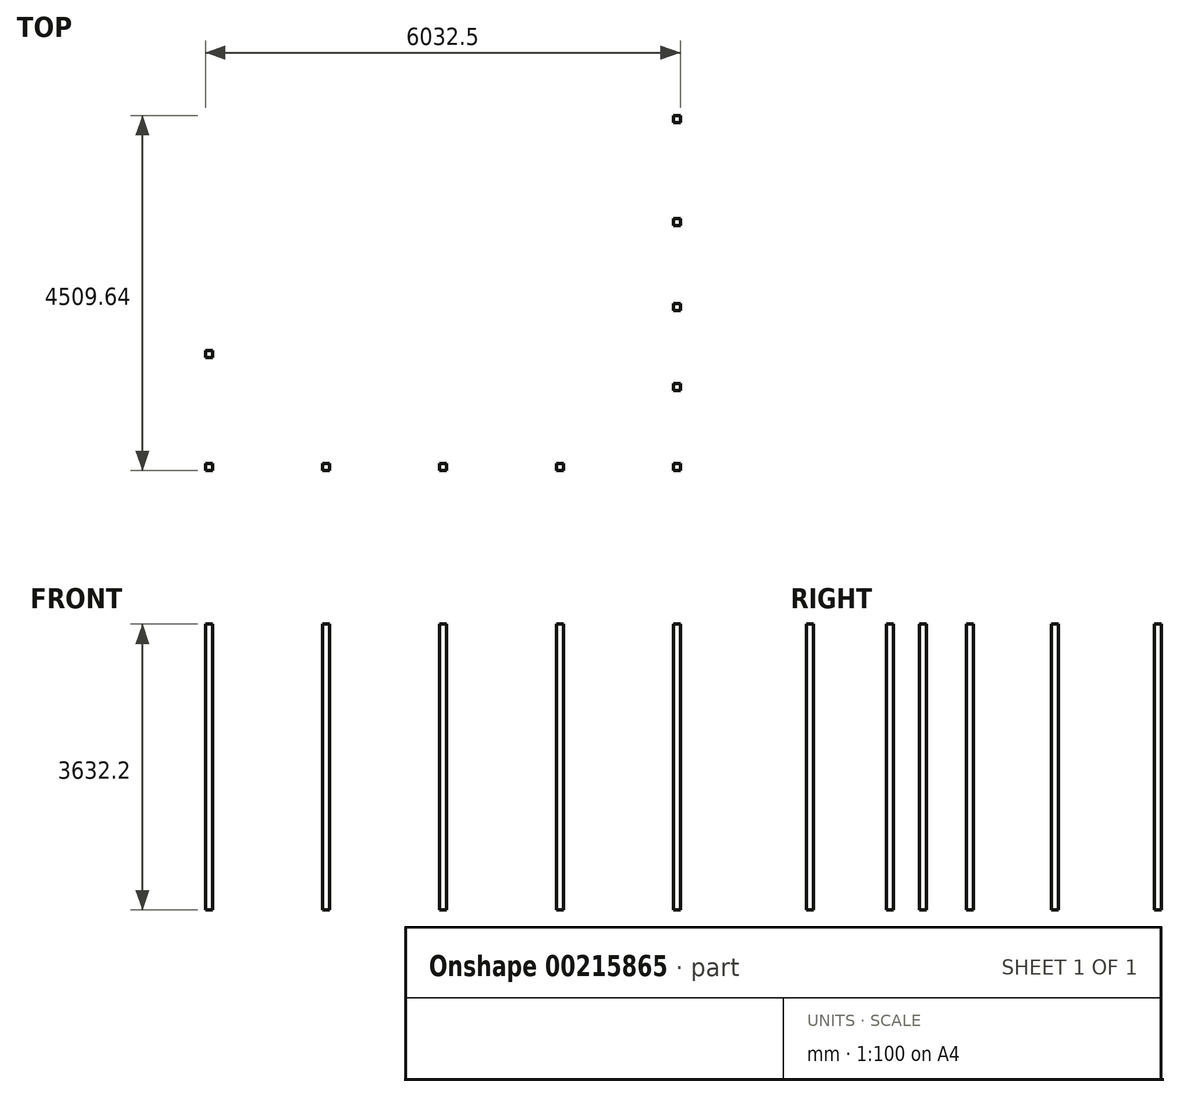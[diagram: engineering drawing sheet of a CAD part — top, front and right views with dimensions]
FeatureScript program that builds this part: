
annotation { "Feature Type Name" : "Feature", "Feature Type Description" : "" }
export const myFeature = defineFeature(function(context is Context, id is Id, definition is map)
    precondition{}
    {
        {
            var Q0;
            Q0=qCreatedBy(makeId("Top.planeOp"),FACE);
            var sketch = newSketch(context, id + "F0", { "sketchPlane" : qUnion([Q0])});
            skLineSegment(sketch, "E0.bottom", {"start": v(0, 0) * mm, "end": v(-88.9, 0) * mm});
            skLineSegment(sketch, "E0.top", {"start": v(0, 88.9) * mm, "end": v(-88.9, 88.9) * mm});
            skLineSegment(sketch, "E0.left", {"start": v(0, 0) * mm, "end": v(0, 88.9) * mm});
            skLineSegment(sketch, "E0.right", {"start": v(-88.9, 0) * mm, "end": v(-88.9, 88.9) * mm});
            skLineSegment(sketch, "E1.bottom", {"start": v(-1485.9, 0) * mm, "end": v(-1574.8, 0) * mm});
            skLineSegment(sketch, "E1.top", {"start": v(-1485.9, 88.9) * mm, "end": v(-1574.8, 88.9) * mm});
            skLineSegment(sketch, "E1.left", {"start": v(-1485.9, 0) * mm, "end": v(-1485.9, 88.9) * mm});
            skLineSegment(sketch, "E1.right", {"start": v(-1574.8, 0) * mm, "end": v(-1574.8, 88.9) * mm});
            skLineSegment(sketch, "E2.bottom", {"start": v(-2971.8, 0) * mm, "end": v(-3060.7, 0) * mm});
            skLineSegment(sketch, "E2.top", {"start": v(-2971.8, 88.9) * mm, "end": v(-3060.7, 88.9) * mm});
            skLineSegment(sketch, "E2.left", {"start": v(-2971.8, 0) * mm, "end": v(-2971.8, 88.9) * mm});
            skLineSegment(sketch, "E2.right", {"start": v(-3060.7, 0) * mm, "end": v(-3060.7, 88.9) * mm});
            skLineSegment(sketch, "E3.bottom", {"start": v(-4457.7, 0) * mm, "end": v(-4546.6, 0) * mm});
            skLineSegment(sketch, "E3.top", {"start": v(-4457.7, 88.9) * mm, "end": v(-4546.6, 88.9) * mm});
            skLineSegment(sketch, "E3.left", {"start": v(-4457.7, 0) * mm, "end": v(-4457.7, 88.9) * mm});
            skLineSegment(sketch, "E3.right", {"start": v(-4546.6, 0) * mm, "end": v(-4546.6, 88.9) * mm});
            skLineSegment(sketch, "E4.bottom", {"start": v(-5943.6, 0) * mm, "end": v(-6032.5, 0) * mm});
            skLineSegment(sketch, "E4.top", {"start": v(-5943.6, 88.9) * mm, "end": v(-6032.5, 88.9) * mm});
            skLineSegment(sketch, "E4.left", {"start": v(-5943.6, 0) * mm, "end": v(-5943.6, 88.9) * mm});
            skLineSegment(sketch, "E4.right", {"start": v(-6032.5, 0) * mm, "end": v(-6032.5, 88.9) * mm});
            skLineSegment(sketch, "E5.bottom", {"start": v(-88.9, 1016) * mm, "end": v(0, 1016) * mm});
            skLineSegment(sketch, "E5.top", {"start": v(-88.9, 1104.9) * mm, "end": v(0, 1104.9) * mm});
            skLineSegment(sketch, "E5.left", {"start": v(-88.9, 1016) * mm, "end": v(-88.9, 1104.9) * mm});
            skLineSegment(sketch, "E5.right", {"start": v(0, 1016) * mm, "end": v(0, 1104.9) * mm});
            skLineSegment(sketch, "E6.bottom", {"start": v(-88.9, 2032) * mm, "end": v(0, 2032) * mm});
            skLineSegment(sketch, "E6.top", {"start": v(-88.9, 2120.9) * mm, "end": v(0, 2120.9) * mm});
            skLineSegment(sketch, "E6.left", {"start": v(-88.9, 2032) * mm, "end": v(-88.9, 2120.9) * mm});
            skLineSegment(sketch, "E6.right", {"start": v(0, 2032) * mm, "end": v(0, 2120.9) * mm});
            skLineSegment(sketch, "E7.bottom", {"start": v(-88.9, 4420.74) * mm, "end": v(0, 4420.74) * mm});
            skLineSegment(sketch, "E7.top", {"start": v(-88.9, 4509.64) * mm, "end": v(0, 4509.64) * mm});
            skLineSegment(sketch, "E7.left", {"start": v(-88.9, 4420.74) * mm, "end": v(-88.9, 4509.64) * mm});
            skLineSegment(sketch, "E7.right", {"start": v(0, 4420.74) * mm, "end": v(0, 4509.64) * mm});
            skLineSegment(sketch, "E8.bottom", {"start": v(-6032.5, 1435.1) * mm, "end": v(-5943.6, 1435.1) * mm});
            skLineSegment(sketch, "E8.top", {"start": v(-6032.5, 1524) * mm, "end": v(-5943.6, 1524) * mm});
            skLineSegment(sketch, "E8.left", {"start": v(-6032.5, 1435.1) * mm, "end": v(-6032.5, 1524) * mm});
            skLineSegment(sketch, "E8.right", {"start": v(-5943.6, 1435.1) * mm, "end": v(-5943.6, 1524) * mm});
            skLineSegment(sketch, "E9.bottom", {"start": v(-88.9, 3201.54) * mm, "end": v(0, 3201.54) * mm});
            skLineSegment(sketch, "E9.top", {"start": v(-88.9, 3112.64) * mm, "end": v(0, 3112.64) * mm});
            skLineSegment(sketch, "E9.left", {"start": v(-88.9, 3201.54) * mm, "end": v(-88.9, 3112.64) * mm});
            skLineSegment(sketch, "E9.right", {"start": v(0, 3201.54) * mm, "end": v(0, 3112.64) * mm});
            skSolve(sketch);
        }
        {
            var Q0;
            Q0 = qSketchRegion(id + "F0", true);
            extrude(context, id + "F1", {"entities" : qUnion([Q0]), "depth" : 3632.2 * mm, "offsetDistance" : 25.4 * mm});
        }
    });
